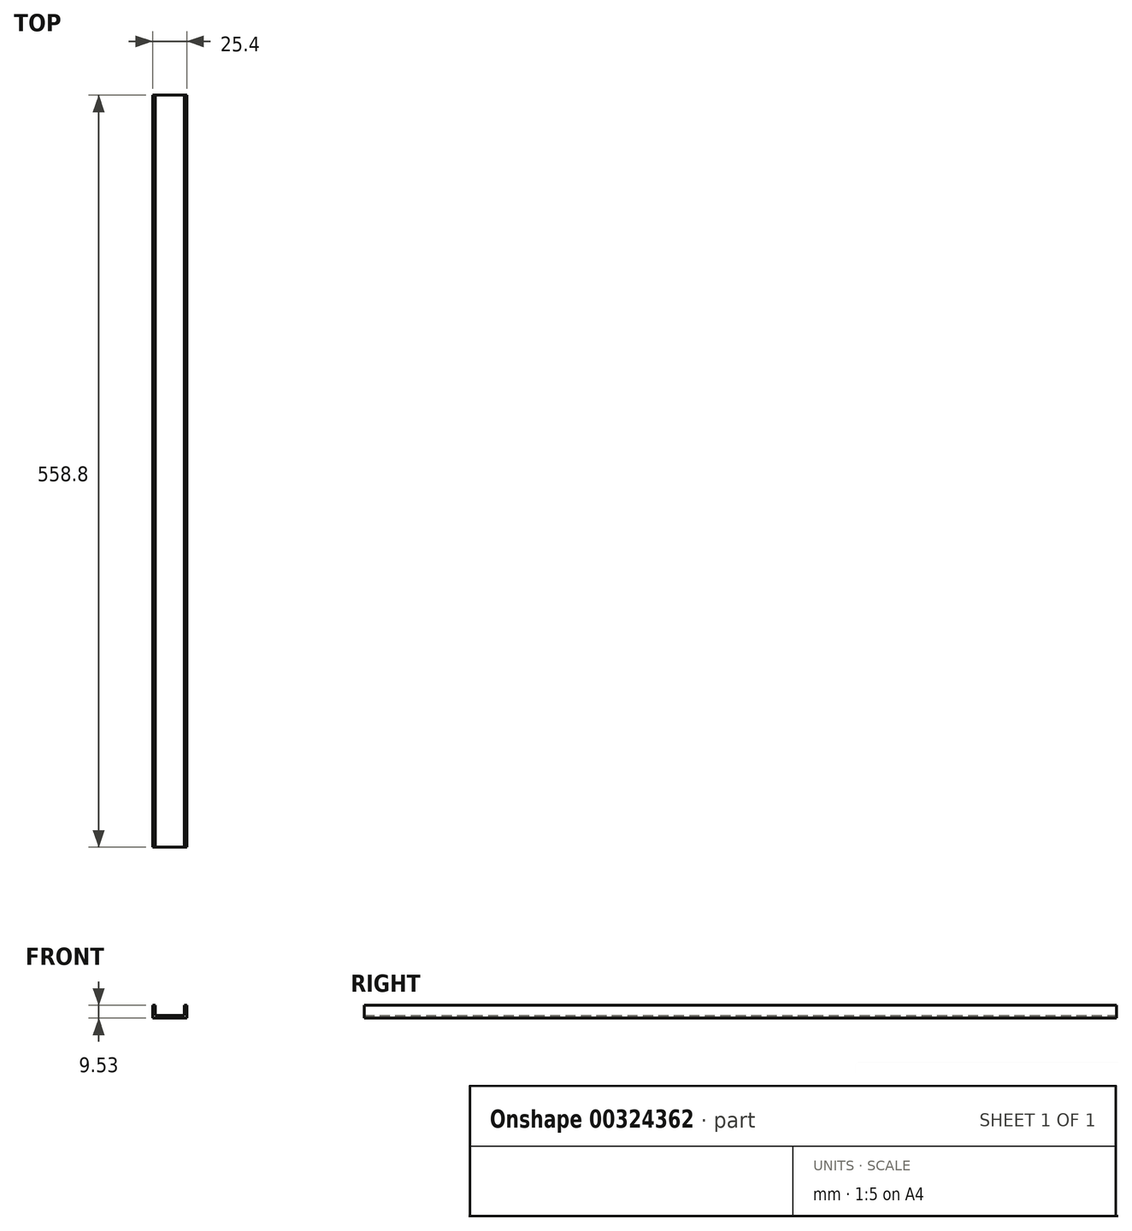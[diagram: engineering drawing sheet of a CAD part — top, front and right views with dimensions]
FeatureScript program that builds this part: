
annotation { "Feature Type Name" : "Feature", "Feature Type Description" : "" }
export const myFeature = defineFeature(function(context is Context, id is Id, definition is map)
    precondition{}
    {
        {
            var Q0;
            Q0=qCreatedBy(makeId("Front.planeOp"),FACE);
            var sketch = newSketch(context, id + "F0", { "sketchPlane" : qUnion([Q0])});
            skLineSegment(sketch, "E0", {"start": v(-12.7, 9.52) * mm, "end": v(-12.7, 0) * mm});
            skLineSegment(sketch, "E1", {"start": v(-12.7, 0) * mm, "end": v(12.7, 0) * mm});
            skLineSegment(sketch, "E2", {"start": v(12.7, 0) * mm, "end": v(12.7, 9.53) * mm});
            skLineSegment(sketch, "E3", {"start": v(12.7, 9.53) * mm, "end": v(10.8, 9.53) * mm});
            skLineSegment(sketch, "E4", {"start": v(10.8, 9.53) * mm, "end": v(10.8, 1.9) * mm});
            skLineSegment(sketch, "E5", {"start": v(10.8, 1.9) * mm, "end": v(-10.8, 1.9) * mm});
            skLineSegment(sketch, "E6", {"start": v(-10.8, 1.9) * mm, "end": v(-10.8, 9.52) * mm});
            skLineSegment(sketch, "E7", {"start": v(-10.8, 9.53) * mm, "end": v(-12.7, 9.52) * mm});
            skSolve(sketch);
        }
        {
            var Q0;
            Q0=makeQuery(id+"F0.imprint","IMPRINT",FACE,{"disambiguationData":[TD([[makeQuery(id+"F0.imprint","IMPRINT",EDGE,{"derivedFrom":sQuery(id+"F0.wireOp",EDGE,"E0")}),1.0]])]});
            extrude(context, id + "F1", {"entities" : qUnion([Q0]), "depth" : 558.8 * mm});
        }
    });
